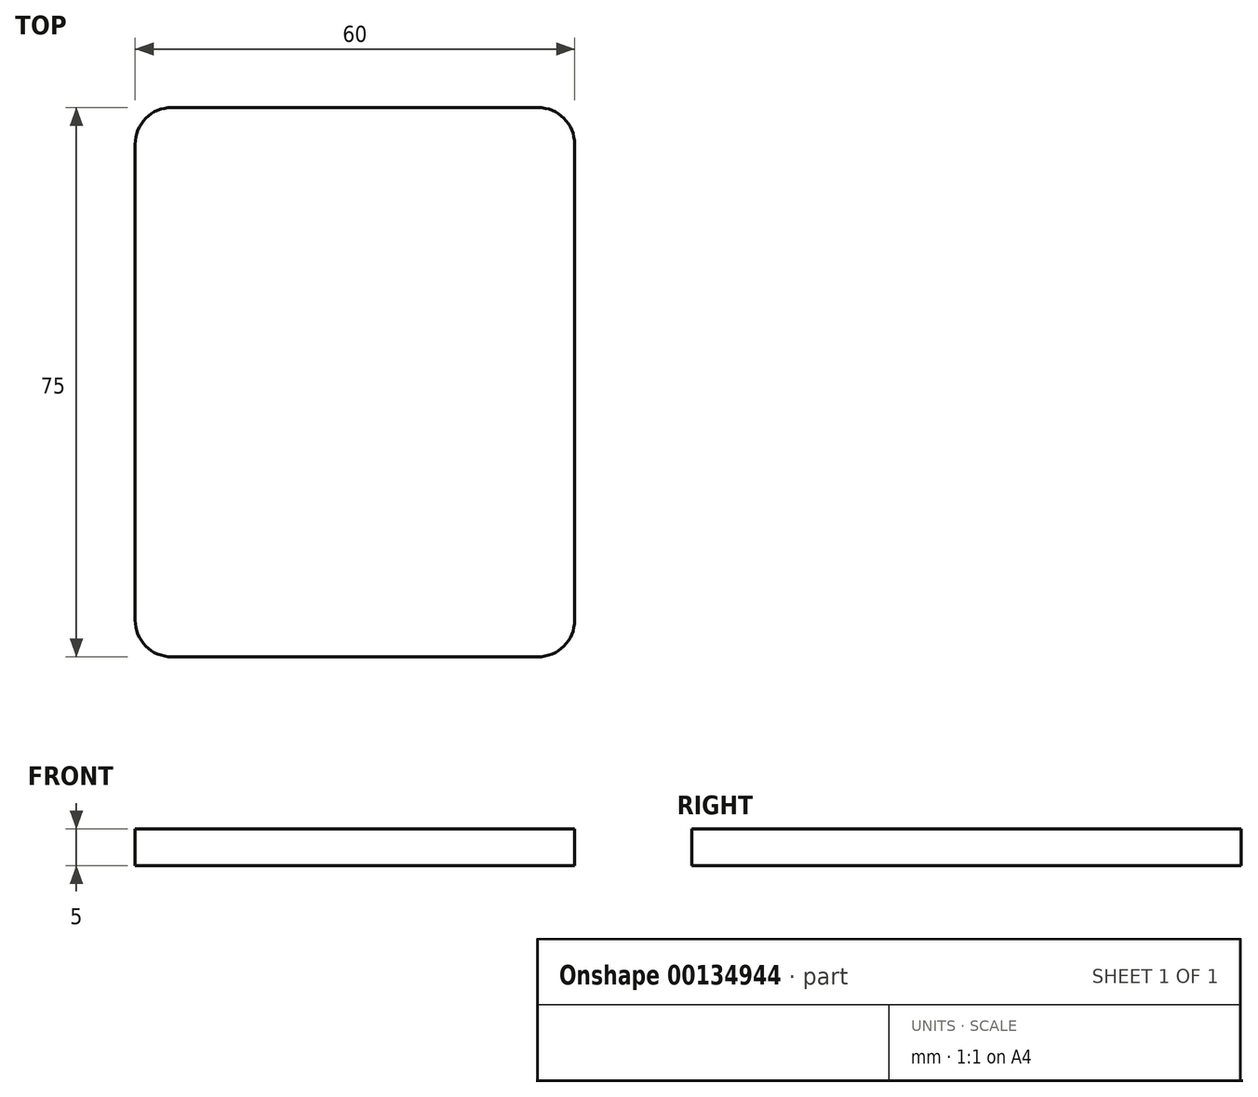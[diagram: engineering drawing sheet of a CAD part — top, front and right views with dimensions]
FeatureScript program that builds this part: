
annotation { "Feature Type Name" : "Feature", "Feature Type Description" : "" }
export const myFeature = defineFeature(function(context is Context, id is Id, definition is map)
    precondition{}
    {
        {
            var Q0;
            Q0=qCreatedBy(makeId("Front.planeOp"),FACE);
            var sketch = newSketch(context, id + "F0", { "sketchPlane" : qUnion([Q0])});
            skLineSegment(sketch, "E0.bottom", {"start": v(0, 0) * mm, "end": v(60, 0) * mm});
            skLineSegment(sketch, "E0.top", {"start": v(0, 5) * mm, "end": v(60, 5) * mm});
            skLineSegment(sketch, "E0.left", {"start": v(0, 0) * mm, "end": v(0, 5) * mm});
            skLineSegment(sketch, "E0.right", {"start": v(60, 0) * mm, "end": v(60, 5) * mm});
            skSolve(sketch);
        }
        {
            var Q0;
            Q0=makeQuery(id+"F0.imprint","IMPRINT",FACE,{"disambiguationData":[TD([[makeQuery(id+"F0.imprint","IMPRINT",EDGE,{"derivedFrom":sQuery(id+"F0.wireOp",EDGE,"E0.bottom")}),1.0]])]});
            extrude(context, id + "F1", {"entities" : qUnion([Q0]), "depth" : 75 * mm});
        }
        {
            var Q0;
            Q0=makeQuery(id+"F1.opExtrude","CAP_EDGE",EDGE,{"disambiguationData":[OSD([sQuery(id+"F0.wireOp",EDGE,"E0.right")])],"isStart":false});
            var Q1;
            Q1=makeQuery(id+"F1.opExtrude","CAP_EDGE",EDGE,{"disambiguationData":[OSD([sQuery(id+"F0.wireOp",EDGE,"E0.right")])],"isStart":true});
            var Q2;
            Q2=makeQuery(id+"F1.opExtrude","CAP_EDGE",EDGE,{"disambiguationData":[OSD([sQuery(id+"F0.wireOp",EDGE,"E0.left")])],"isStart":true});
            var Q3;
            Q3=makeQuery(id+"F1.opExtrude","CAP_EDGE",EDGE,{"disambiguationData":[OSD([sQuery(id+"F0.wireOp",EDGE,"E0.left")])],"isStart":false});
            fillet(context, id + "F2", {"entities" : qUnion([Q0, Q1, Q2, Q3]), "radius" : 5 * mm, "tangentPropagation" : true, "allowEdgeOverflow" : false});
        }
    });
